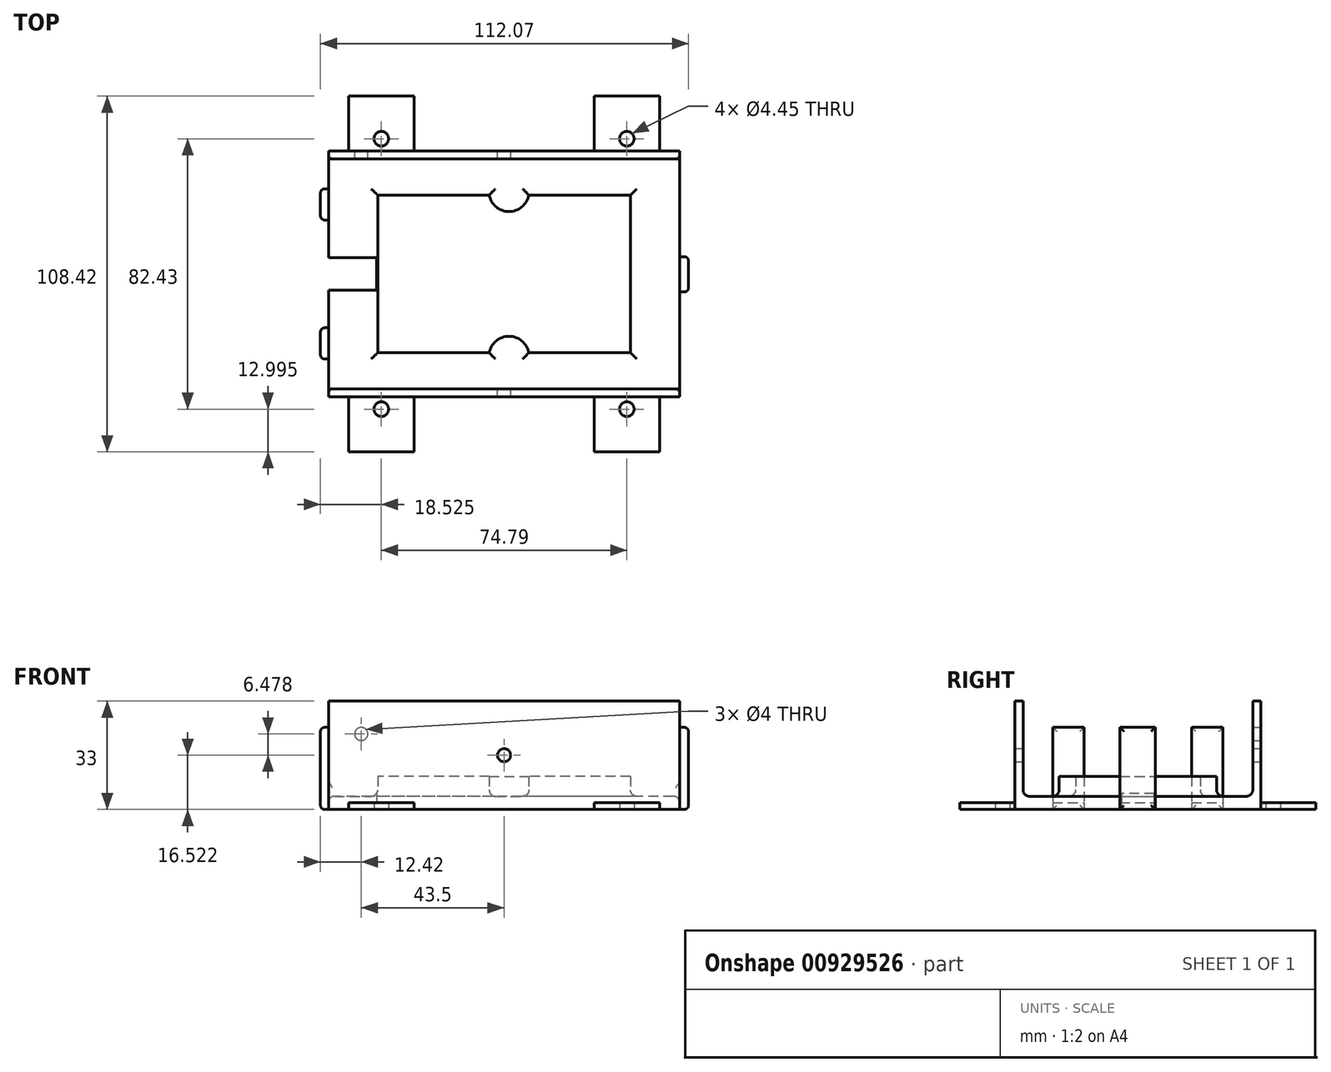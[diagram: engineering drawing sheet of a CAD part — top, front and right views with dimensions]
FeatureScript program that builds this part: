
annotation { "Feature Type Name" : "Feature", "Feature Type Description" : "" }
export const myFeature = defineFeature(function(context is Context, id is Id, definition is map)
    precondition{}
    {
        {
            var Q0;
            Q0=qCreatedBy(makeId("Top.planeOp"),FACE);
            var sketch = newSketch(context, id + "F0", { "sketchPlane" : qUnion([Q0])});
            skLineSegment(sketch, "E0.bottom", {"start": v(53.5, -37.5) * mm, "end": v(-53.5, -37.5) * mm});
            skLineSegment(sketch, "E0.top", {"start": v(53.5, 37.5) * mm, "end": v(-53.5, 37.5) * mm});
            skLineSegment(sketch, "E0.left", {"start": v(53.5, -37.5) * mm, "end": v(53.5, 37.5) * mm});
            skLineSegment(sketch, "E0.right", {"start": v(-53.5, -37.5) * mm, "end": v(-53.5, 37.5) * mm});
            skPoint(sketch, "E0.middle", {"position": v(0, 0) * mm});
            skLineSegment(sketch, "E1.bottom", {"start": v(53.5, -35) * mm, "end": v(-53.5, -35) * mm});
            skLineSegment(sketch, "E1.top", {"start": v(53.5, 35) * mm, "end": v(-53.5, 35) * mm});
            skLineSegment(sketch, "E1.left", {"start": v(53.5, -35) * mm, "end": v(53.5, 35) * mm});
            skLineSegment(sketch, "E1.right", {"start": v(-53.5, -35) * mm, "end": v(-53.5, 35) * mm});
            skLineSegment(sketch, "E2.bottom", {"start": v(38.5, -24) * mm, "end": v(7.5, -24) * mm});
            skLineSegment(sketch, "E2.top", {"start": v(38.5, 24) * mm, "end": v(7.5, 24) * mm});
            skLineSegment(sketch, "E2.left", {"start": v(38.5, -24) * mm, "end": v(38.5, 24) * mm});
            skLineSegment(sketch, "E2.right", {"start": v(-38.5, -24) * mm, "end": v(-38.5, 24) * mm});
            skArc(sketch, "E3", {"start": v(7.5, -24) * mm, "mid": v(1.5, -19) * mm, "end": v(-4.5, -24) * mm});
            skPoint(sketch, "E4", {"position": v(1.5, -19) * mm});
            skLineSegment(sketch, "E5", {"start": v(-65.93, 0) * mm, "end": v(67.65, 0) * mm, "construction": true});
            skArc(sketch, "E6.MirrorCS", {"start": v(7.5, 24) * mm, "mid": v(1.5, 19) * mm, "end": v(-4.5, 24) * mm});
            skLineSegment(sketch, "E7.trimOffspring", {"start": v(-4.5, 24) * mm, "end": v(-38.5, 24) * mm});
            skLineSegment(sketch, "E8.trimOffspring", {"start": v(-4.5, -24) * mm, "end": v(-38.5, -24) * mm});
            skLineSegment(sketch, "E9.bottom", {"start": v(-53.5, 25.94) * mm, "end": v(-55.92, 25.94) * mm});
            skLineSegment(sketch, "E9.top", {"start": v(-53.5, 16.43) * mm, "end": v(-55.92, 16.43) * mm});
            skLineSegment(sketch, "E9.left", {"start": v(-53.5, 25.94) * mm, "end": v(-53.5, 16.43) * mm});
            skLineSegment(sketch, "E9.right", {"start": v(-55.92, 25.94) * mm, "end": v(-55.92, 16.43) * mm});
            skLineSegment(sketch, "E10.bottom", {"start": v(53.5, 5.26) * mm, "end": v(56.15, 5.26) * mm});
            skLineSegment(sketch, "E10.top", {"start": v(53.5, -5.48) * mm, "end": v(56.15, -5.48) * mm});
            skLineSegment(sketch, "E10.left", {"start": v(53.5, 5.26) * mm, "end": v(53.5, -5.48) * mm});
            skLineSegment(sketch, "E10.right", {"start": v(56.15, 5.26) * mm, "end": v(56.15, -5.48) * mm});
            skLineSegment(sketch, "E11.MirrorCS", {"start": v(-53.5, -16.43) * mm, "end": v(-55.92, -16.43) * mm});
            skLineSegment(sketch, "E12.MirrorCS", {"start": v(-55.92, -25.94) * mm, "end": v(-55.92, -16.43) * mm});
            skLineSegment(sketch, "E13.MirrorCS", {"start": v(-53.5, -25.94) * mm, "end": v(-55.92, -25.94) * mm});
            skSolve(sketch);
        }
        {
            var Q0;
            Q0=makeQuery(id+"F0.imprint","IMPRINT",FACE,{"disambiguationData":[TD([[makeQuery(id+"F0.imprint","IMPRINT",EDGE,{"derivedFrom":sQuery(id+"F0.wireOp",EDGE,"E1.bottom")}),-1.0]])]});
            extrude(context, id + "F1", {"entities" : qUnion([Q0]), "depth" : 4 * mm, "offsetDistance" : 25 * mm});
        }
        {
            var Q0;
            {var subQ0=sQuery(id+"F0.wireOp",EDGE,"E0.top");Q0=makeQuery(id+"F0.imprint","IMPRINT",FACE,{"disambiguationData":[TD([[makeQuery(id+"F0.imprint","IMPRINT",EDGE,{"derivedFrom":subQ0}),1.0]])]});}
            var Q1;
            {var subQ0=sQuery(id+"F0.wireOp",EDGE,"E0.bottom");Q1=makeQuery(id+"F0.imprint","IMPRINT",FACE,{"disambiguationData":[TD([[makeQuery(id+"F0.imprint","IMPRINT",EDGE,{"derivedFrom":subQ0}),-1.0]])]});}
            extrude(context, id + "F2", {"entities" : qUnion([Q0, Q1]), "operationType" : NewBodyOperationType.ADD, "depth" : 33 * mm, "offsetDistance" : 25 * mm});
        }
        {
            var Q0;
            Q0=makeQuery(id+"F0.imprint","IMPRINT",FACE,{"disambiguationData":[TD([[makeQuery(id+"F0.imprint","IMPRINT",EDGE,{"derivedFrom":sQuery(id+"F0.wireOp",EDGE,"E1.bottom")}),-1.0]])]});
            var sketch = newSketch(context, id + "F3", { "sketchPlane" : qUnion([Q0])});
            skLineSegment(sketch, "E14.bottom", {"start": v(-27.4, -28.21) * mm, "end": v(-47.4, -28.21) * mm});
            skLineSegment(sketch, "E14.top", {"start": v(-27.4, -54.22) * mm, "end": v(-47.4, -54.21) * mm});
            skLineSegment(sketch, "E14.left", {"start": v(-27.4, -28.21) * mm, "end": v(-27.4, -54.22) * mm});
            skLineSegment(sketch, "E14.right", {"start": v(-47.4, -28.21) * mm, "end": v(-47.4, -54.21) * mm});
            skPoint(sketch, "E14.middle", {"position": v(-37.4, -41.21) * mm});
            skLineSegment(sketch, "E15", {"start": v(-60.28, 0) * mm, "end": v(70.34, 0) * mm, "construction": true});
            skLineSegment(sketch, "E16", {"start": v(0, -45) * mm, "end": v(0, 55.82) * mm, "construction": true});
            skPoint(sketch, "E17.MirrorP", {"position": v(-37.4, 41.21) * mm});
            skLineSegment(sketch, "E18.MirrorCS", {"start": v(-27.4, 28.21) * mm, "end": v(-27.4, 54.22) * mm});
            skLineSegment(sketch, "E19.MirrorCS", {"start": v(-27.4, 28.21) * mm, "end": v(-47.4, 28.21) * mm});
            skLineSegment(sketch, "E20.MirrorCS", {"start": v(-47.4, 28.21) * mm, "end": v(-47.4, 54.21) * mm});
            skLineSegment(sketch, "E21.MirrorCS", {"start": v(-27.4, 54.22) * mm, "end": v(-47.4, 54.22) * mm});
            skLineSegment(sketch, "E22.MirrorCS", {"start": v(27.4, -28.21) * mm, "end": v(27.4, -54.22) * mm});
            skLineSegment(sketch, "E23.MirrorCS", {"start": v(27.4, -54.22) * mm, "end": v(47.4, -54.22) * mm});
            skLineSegment(sketch, "E24.MirrorCS", {"start": v(47.4, -28.21) * mm, "end": v(47.4, -54.21) * mm});
            skLineSegment(sketch, "E25.MirrorCS", {"start": v(27.4, -28.21) * mm, "end": v(47.4, -28.21) * mm});
            skLineSegment(sketch, "E26.MirrorCS", {"start": v(27.4, 28.21) * mm, "end": v(47.4, 28.21) * mm});
            skLineSegment(sketch, "E27.MirrorCS", {"start": v(27.4, 28.21) * mm, "end": v(27.4, 54.22) * mm});
            skLineSegment(sketch, "E28.MirrorCS", {"start": v(27.4, 54.22) * mm, "end": v(47.4, 54.22) * mm});
            skLineSegment(sketch, "E29.MirrorCS", {"start": v(47.4, 28.21) * mm, "end": v(47.4, 54.21) * mm});
            skCircle(sketch, "E30", {"center": v(-37.4, -41.21) * mm, "radius": 2.22 * mm});
            skCircle(sketch, "E31.MirrorC", {"center": v(-37.4, 41.21) * mm, "radius": 2.22 * mm});
            skPoint(sketch, "E32.MirrorP", {"position": v(37.4, 41.21) * mm});
            skCircle(sketch, "E33.MirrorC", {"center": v(37.4, 41.21) * mm, "radius": 2.22 * mm});
            skCircle(sketch, "E34.MirrorC", {"center": v(37.4, -41.21) * mm, "radius": 2.22 * mm});
            skSolve(sketch);
        }
        {
            var Q0;
            {var subQ0=sQuery(id+"F3.wireOp",EDGE,"E14.top");Q0=makeQuery(id+"F3.imprint","IMPRINT",FACE,{"disambiguationData":[TD([[makeQuery(id+"F3.imprint","IMPRINT",EDGE,{"derivedFrom":subQ0}),-1.0]])]});}
            var Q1;
            {var subQ0=sQuery(id+"F3.wireOp",EDGE,"E23.MirrorCS");Q1=makeQuery(id+"F3.imprint","IMPRINT",FACE,{"disambiguationData":[TD([[makeQuery(id+"F3.imprint","IMPRINT",EDGE,{"derivedFrom":subQ0}),1.0]])]});}
            var Q2;
            {var subQ0=sQuery(id+"F3.wireOp",EDGE,"E28.MirrorCS");Q2=makeQuery(id+"F3.imprint","IMPRINT",FACE,{"disambiguationData":[TD([[makeQuery(id+"F3.imprint","IMPRINT",EDGE,{"derivedFrom":subQ0}),-1.0]])]});}
            var Q3;
            {var subQ0=sQuery(id+"F3.wireOp",EDGE,"E21.MirrorCS");Q3=makeQuery(id+"F3.imprint","IMPRINT",FACE,{"disambiguationData":[TD([[makeQuery(id+"F3.imprint","IMPRINT",EDGE,{"derivedFrom":subQ0}),1.0]])]});}
            extrude(context, id + "F4", {"entities" : qUnion([Q0, Q1, Q2, Q3]), "operationType" : NewBodyOperationType.ADD, "depth" : 2 * mm, "offsetDistance" : 25 * mm});
        }
        {
            var Q0;
            Q0=makeQuery(id+"F2.opExtrude","SWEPT_FACE",FACE,{"disambiguationData":[OSD([sQuery(id+"F0.wireOp",EDGE,"E0.top")])]});
            var sketch = newSketch(context, id + "F5", { "sketchPlane" : qUnion([Q0])});
            skCircle(sketch, "E35", {"center": v(43.5, 23) * mm, "radius": 1.76 * mm});
            skCircle(sketch, "E36", {"center": v(0, 16.52) * mm, "radius": 2.2 * mm});
            skSolve(sketch);
        }
        {
            var Q0;
            Q0=sQuery(id+"F5.wireOp",VERTEX,"E35.center");
            var Q1;
            Q1=makeQuery(id+"F1.opExtrude","SWEPT_BODY",BODY,{"disambiguationData":[OSD([sQuery(id+"F0.wireOp",EDGE,"E1.bottom"),sQuery(id+"F0.wireOp",EDGE,"E1.top"),sQuery(id+"F0.wireOp",EDGE,"E1.left"),sQuery(id+"F0.wireOp",EDGE,"E1.right")])]});
            hole(context, id + "F6", {"style" : HoleStyle.SIMPLE, "endStyle" : HoleEndStyle.BLIND, "holeDiameter" : 4 * mm, "majorDiameter" : 5 * mm, "holeDepth" : 12 * mm, "isTappedThrough" : true, "tappedDepth" : 12 * mm, "tapClearance" : 3, "locations" : qUnion([Q0]), "scope" : qUnion([Q1])});
        }
        {
            var Q0;
            Q0=sQuery(id+"F5.wireOp",VERTEX,"E36.center");
            var Q1;
            Q1=makeQuery(id+"F1.opExtrude","SWEPT_BODY",BODY,{"disambiguationData":[OSD([sQuery(id+"F0.wireOp",EDGE,"E1.bottom"),sQuery(id+"F0.wireOp",EDGE,"E1.top"),sQuery(id+"F0.wireOp",EDGE,"E1.left"),sQuery(id+"F0.wireOp",EDGE,"E1.right")])]});
            hole(context, id + "F7", {"style" : HoleStyle.SIMPLE, "endStyle" : HoleEndStyle.THROUGH, "holeDiameter" : 4 * mm, "majorDiameter" : 5 * mm, "isTappedThrough" : true, "tappedDepth" : 12 * mm, "tapClearance" : 3, "locations" : qUnion([Q0]), "scope" : qUnion([Q1])});
        }
        {
            var Q0;
            Q0=makeQuery(id+"F0.imprint","IMPRINT",FACE,{"disambiguationData":[TD([[makeQuery(id+"F0.imprint","IMPRINT",EDGE,{"derivedFrom":sQuery(id+"F0.wireOp",EDGE,"E2.bottom")}),-1.0]])]});
            extrude(context, id + "F8", {"entities" : qUnion([Q0]), "operationType" : NewBodyOperationType.ADD, "depth" : 10 * mm, "offsetDistance" : 25 * mm});
        }
        {
            var Q0;
            Q0=makeQuery(id+"F1.opExtrude","CAP_FACE",FACE,{"disambiguationData":[OSD([sQuery(id+"F0.wireOp",EDGE,"E1.bottom"),sQuery(id+"F0.wireOp",EDGE,"E1.top"),sQuery(id+"F0.wireOp",EDGE,"E1.left"),sQuery(id+"F0.wireOp",EDGE,"E1.right"),sQuery(id+"F0.wireOp",EDGE,"E2.bottom"),sQuery(id+"F0.wireOp",EDGE,"E2.top"),sQuery(id+"F0.wireOp",EDGE,"E2.left"),sQuery(id+"F0.wireOp",EDGE,"E2.right"),sQuery(id+"F0.wireOp",EDGE,"E3"),sQuery(id+"F0.wireOp",EDGE,"E6.MirrorCS"),sQuery(id+"F0.wireOp",EDGE,"E7.trimOffspring"),sQuery(id+"F0.wireOp",EDGE,"E8.trimOffspring")])],"isStart":false});
            fillet(context, id + "F9", {"entities" : qUnion([Q0]), "radius" : 1.93 * mm, "tangentPropagation" : true, "allowEdgeOverflow" : false});
        }
        {
            var Q0;
            Q0=makeQuery(id+"F0.imprint","IMPRINT",FACE,{"disambiguationData":[TD([[makeQuery(id+"F0.imprint","IMPRINT",EDGE,{"derivedFrom":sQuery(id+"F0.wireOp",EDGE,"E1.bottom")}),-1.0]])]});
            var sketch = newSketch(context, id + "F10", { "sketchPlane" : qUnion([Q0])});
            skLineSegment(sketch, "E37.bottom", {"start": v(-38.81, 5) * mm, "end": v(-53.81, 5) * mm});
            skLineSegment(sketch, "E37.top", {"start": v(-38.81, -5) * mm, "end": v(-53.81, -5) * mm});
            skLineSegment(sketch, "E37.left", {"start": v(-38.81, 5) * mm, "end": v(-38.81, -5) * mm});
            skLineSegment(sketch, "E37.right", {"start": v(-53.81, 5) * mm, "end": v(-53.81, -5) * mm});
            skPoint(sketch, "E37.middle", {"position": v(-46.31, 0) * mm});
            skSolve(sketch);
        }
        {
            var Q0;
            Q0 = qSketchRegion(id + "F10", true);
            extrude(context, id + "F11", {"entities" : qUnion([Q0]), "operationType" : NewBodyOperationType.REMOVE, "depth" : 11.3 * mm, "offsetDistance" : 25 * mm});
        }
        {
            var Q0;
            Q0=makeQuery(id+"F0.imprint","IMPRINT",FACE,{"disambiguationData":[TD([[makeQuery(id+"F0.imprint","IMPRINT",EDGE,{"derivedFrom":sQuery(id+"F0.wireOp",EDGE,"E9.bottom")}),1.0]])]});
            var Q1;
            {var subQ0=sQuery(id+"F0.wireOp",EDGE,"E11.MirrorCS");Q1=makeQuery(id+"F0.imprint","IMPRINT",FACE,{"disambiguationData":[TD([[makeQuery(id+"F0.imprint","IMPRINT",EDGE,{"derivedFrom":subQ0}),1.0]])]});}
            var Q2;
            Q2=makeQuery(id+"F0.imprint","IMPRINT",FACE,{"disambiguationData":[TD([[makeQuery(id+"F0.imprint","IMPRINT",EDGE,{"derivedFrom":sQuery(id+"F0.wireOp",EDGE,"E10.bottom")}),-1.0]])]});
            extrude(context, id + "F12", {"entities" : qUnion([Q0, Q1, Q2]), "operationType" : NewBodyOperationType.ADD, "depth" : 25 * mm, "offsetDistance" : 25 * mm});
        }
        {
            var Q0;
            Q0=makeQuery(id+"F12.opExtrude","SWEPT_FACE",FACE,{"disambiguationData":[OSD([sQuery(id+"F0.wireOp",EDGE,"E9.right")])]});
            var Q1;
            Q1=makeQuery(id+"F12.opExtrude","SWEPT_FACE",FACE,{"disambiguationData":[OSD([sQuery(id+"F0.wireOp",EDGE,"E12.MirrorCS")])]});
            var Q2;
            Q2=makeQuery(id+"F12.opExtrude","SWEPT_FACE",FACE,{"disambiguationData":[OSD([sQuery(id+"F0.wireOp",EDGE,"E10.right")])]});
            fillet(context, id + "F13", {"entities" : qUnion([Q0, Q1, Q2]), "radius" : 1.2 * mm, "tangentPropagation" : true, "allowEdgeOverflow" : false});
        }
    });
